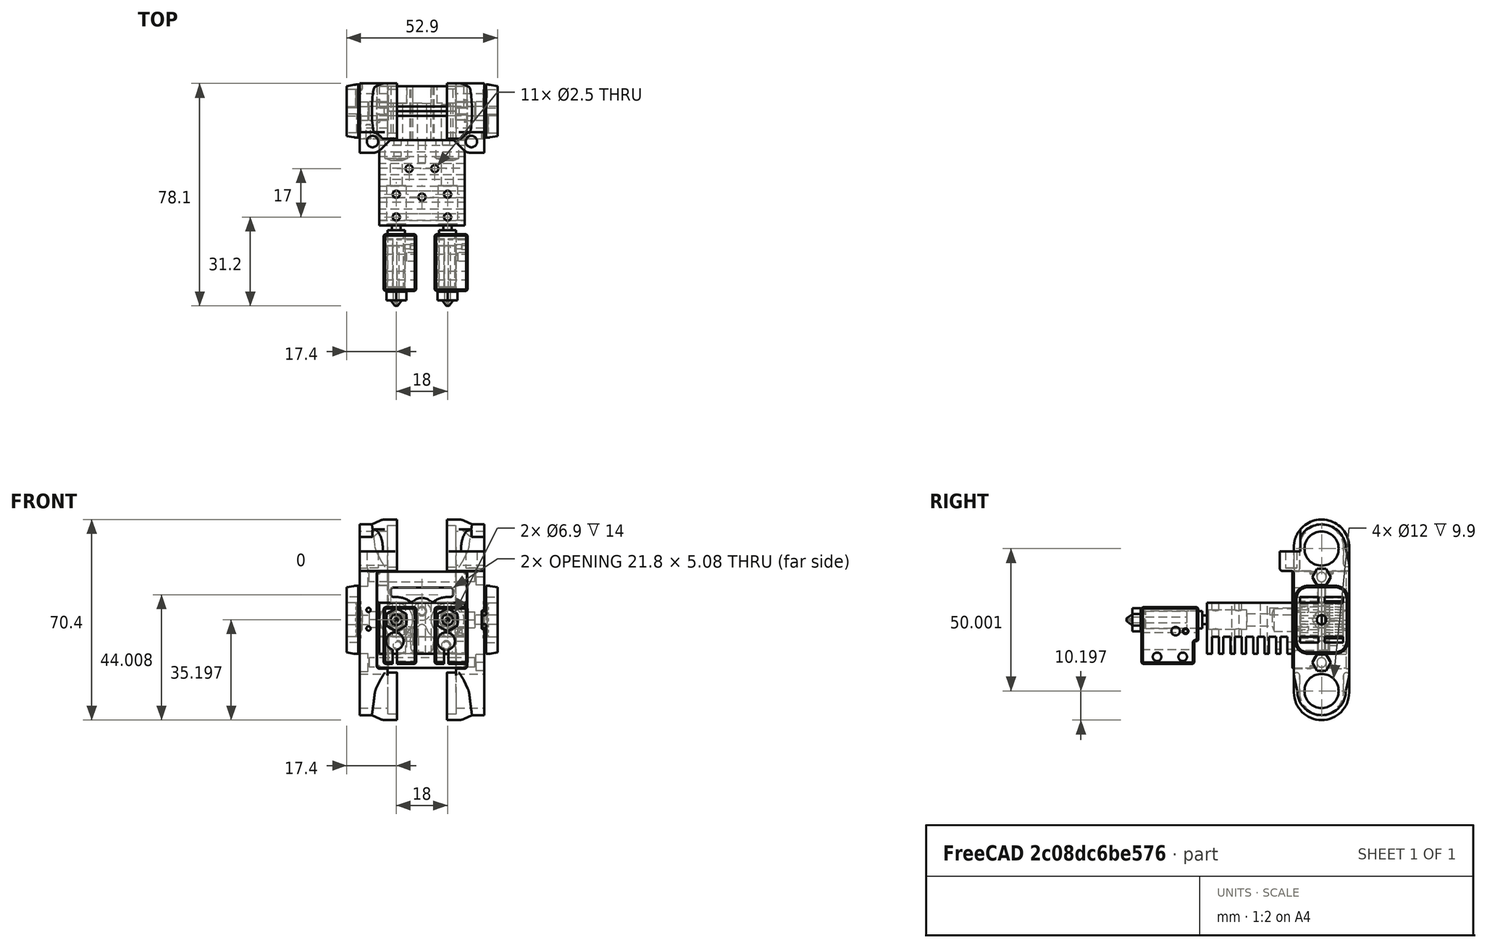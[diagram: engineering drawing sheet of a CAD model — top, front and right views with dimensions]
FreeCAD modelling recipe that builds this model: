
FCSTD DOCUMENT  (FreeCAD 0.17R10423 (Git))
Label: hotend_2
License: All rights reserved
LicenseURL: http://en.wikipedia.org/wiki/All_rights_reserved
objects: Part::Feature×13, Part::Compound×8
note: 21 computed .brp shape members not serialized (recipe doc carries the construction recipe); baked Part::Feature solids carry a one-line shape summary decoded from their .brp

FEATURE [Part::Feature] Part__Feature197  label="Belt Clip"
  Placement = pos=(154.25,385.412,210.347) rot=(0,1,0;1.5708rad)
  shape: bbox 5.4 x 18.6 x 23.9 mm, 83 faces (baked)
FEATURE [Part::Feature] Part__Feature199  label="SOLID006"
  Placement = pos=(126.05,399.5,210.348) rot=(0,-1,0;1.5708rad)
  shape: bbox 13.15 x 25.53 x 72 mm, 176 faces (baked)
FEATURE [Part::Compound] Carriage_End_B
  Links = -> [Part__Feature197,Part__Feature199]
FEATURE [Part::Feature] Part__Feature203  label="Belt Clip001"
  Placement = pos=(154.35,413.588,210.347) rot=(0.707107,0,-0.707107;3.14159rad)
  shape: bbox 5.4 x 18.6 x 23.9 mm, 83 faces (baked)
FEATURE [Part::Feature] Part__Feature208  label="SOLID007"
  Placement = pos=(182.45,399.5,210.347) rot=(0,1,0;1.5708rad)
  shape: bbox 13.15 x 25.53 x 72 mm, 170 faces (baked)
FEATURE [Part::Compound] Carriage_End_A
  Links = -> [Part__Feature203,Part__Feature208]
FEATURE [Part::Feature] Part__Feature215  label="Chimera Heat Sink v2"
  Placement = pos=(154.25,359.3,207.347) rot=(0,0,1;0rad)
  shape: bbox 30 x 30 x 18 mm, 70 faces (baked)
FEATURE [Part::Feature] Part__Feature216  label="E3D Chimera Heat Break v1"
  Placement = pos=(113.25,382.8,210.347) rot=(-0.57735,0.57735,-0.57735;4.18879rad)
  shape: bbox 6.9 x 21.1 x 6.9 mm, 7 faces (baked)
FEATURE [Part::Feature] Part__Feature217  label="E3D Volcano HotEnd Nozzle v2"
  Placement = pos=(163.25,333.1,210.347) rot=(-0.57735,0.57735,-0.57735;4.18879rad)
  shape: bbox 7 x 21.1 x 8.083 mm, 20 faces (baked)
FEATURE [Part::Feature] Part__Feature218  label="Volcano Block v3"
  Placement = pos=(158.75,336.3,194.847) rot=(0.57735,0.57735,0.57735;4.18879rad)
  shape: bbox 11.5 x 20 x 20 mm, 59 faces (baked)
FEATURE [Part::Compound] E3D_Volcano_Heater_Assembly_v2
  Links = -> [Part__Feature216,Part__Feature217,Part__Feature218]
FEATURE [Part::Feature] Part__Feature219  label="E3D Chimera Heat Break v002"
  Placement = pos=(95.25,382.8,210.347) rot=(-0.57735,0.57735,-0.57735;4.18879rad)
  shape: bbox 6.9 x 21.1 x 6.9 mm, 7 faces (baked)
FEATURE [Part::Feature] Part__Feature220  label="E3D Volcano HotEnd Nozzle v003"
  Placement = pos=(145.25,333.1,210.347) rot=(-0.57735,0.57735,-0.57735;4.18879rad)
  shape: bbox 7 x 21.1 x 8.083 mm, 20 faces (baked)
FEATURE [Part::Feature] Part__Feature221  label="Volcano Block v004"
  Placement = pos=(140.75,336.3,194.847) rot=(0.57735,0.57735,0.57735;4.18879rad)
  shape: bbox 11.5 x 20 x 20 mm, 59 faces (baked)
FEATURE [Part::Compound] E3D_Volcano_Heater_Assembly_v2001
  Links = -> [Part__Feature219,Part__Feature220,Part__Feature221]
FEATURE [Part::Feature] Part__Feature225  label="COMPOUND026"
  Placement = pos=(154.25,385.412,210.347) rot=(0,1,0;1.5708rad)
  shape: bbox 31.4 x 10.2 x 33.9 mm, 78 faces (baked)
FEATURE [Part::Feature] Part__Feature226  label="COMPOUND027"
  Placement = pos=(154.25,385.412,210.347) rot=(0,1,0;1.5708rad)
  shape: bbox 31.4 x 8.702 x 33.9 mm, 83 faces (baked)
FEATURE [Part::Compound] COMPOUND007  label="COMPOUND025"
  Links = -> [Part__Feature225,Part__Feature226]
FEATURE [Part::Compound] Chimera_Mount
  Links = -> [COMPOUND007]
FEATURE [Part::Compound] Dual_Extruder
  Links = -> [Part__Feature215,E3D_Volcano_Heater_Assembly_v2,E3D_Volcano_Heater_Assembly_v2001,Chimera_Mount]
FEATURE [Part::Compound] X_Carriage
  Links = -> [Carriage_End_B,Carriage_End_A,Dual_Extruder]
